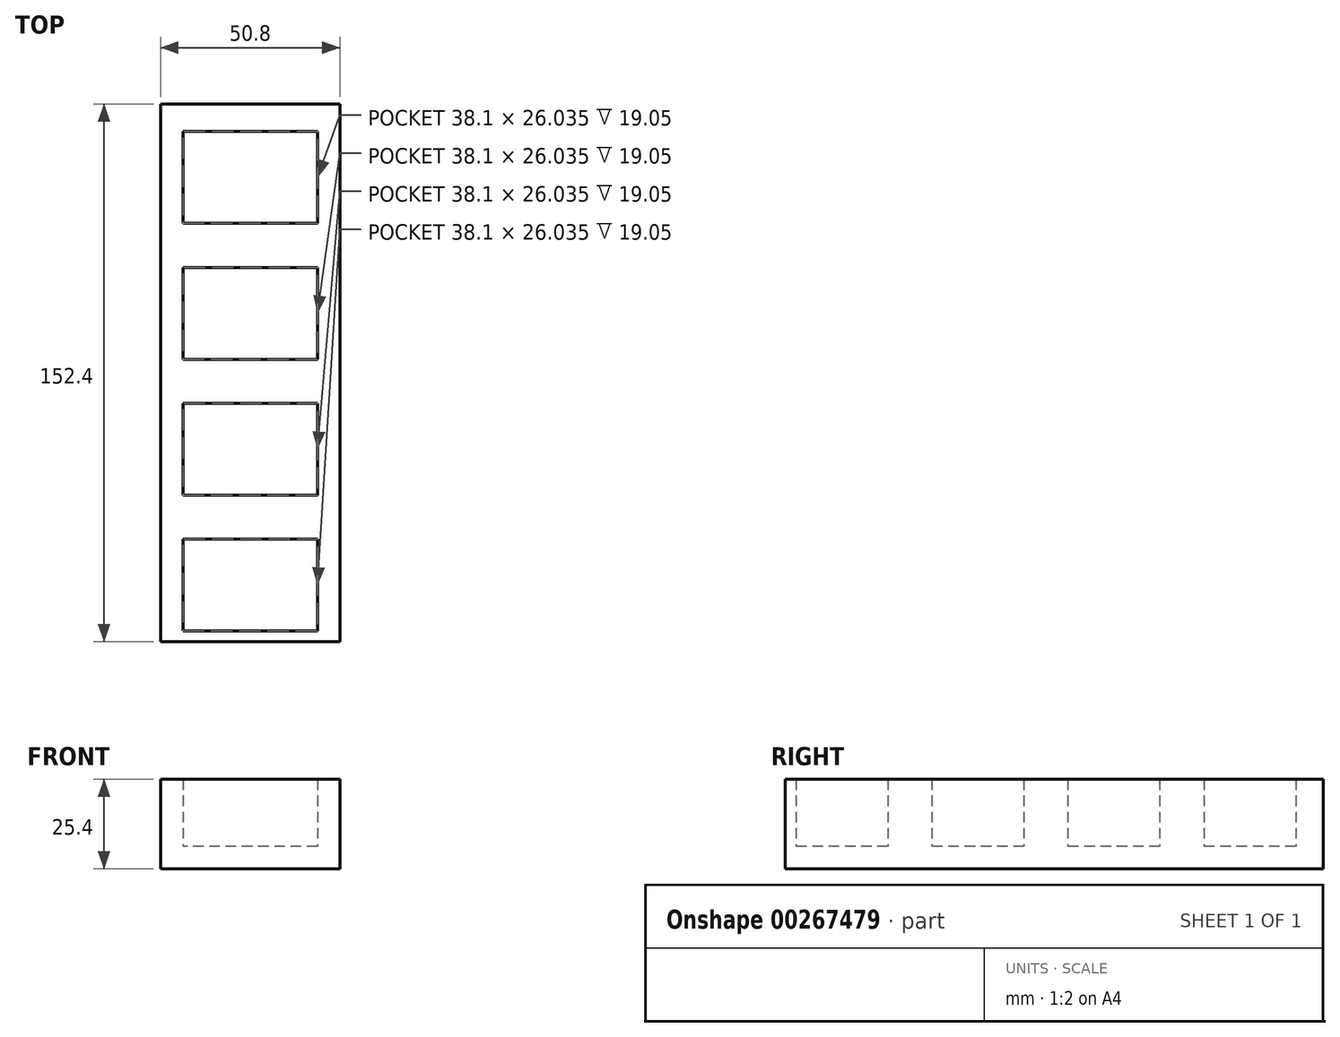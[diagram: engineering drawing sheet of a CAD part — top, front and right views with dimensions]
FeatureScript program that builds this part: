
annotation { "Feature Type Name" : "Feature", "Feature Type Description" : "" }
export const myFeature = defineFeature(function(context is Context, id is Id, definition is map)
    precondition{}
    {
        {
            var Q0;
            Q0=qCreatedBy(makeId("Top.planeOp"),FACE);
            var sketch = newSketch(context, id + "F0", { "sketchPlane" : qUnion([Q0])});
            skLineSegment(sketch, "E0.bottom", {"start": v(25.4, 76.2) * mm, "end": v(-25.4, 76.2) * mm});
            skLineSegment(sketch, "E0.top", {"start": v(25.4, -76.2) * mm, "end": v(-25.4, -76.2) * mm});
            skLineSegment(sketch, "E0.left", {"start": v(25.4, 76.2) * mm, "end": v(25.4, -76.2) * mm});
            skLineSegment(sketch, "E0.right", {"start": v(-25.4, 76.2) * mm, "end": v(-25.4, -76.2) * mm});
            skPoint(sketch, "E0.middle", {"position": v(0, 0) * mm});
            skLineSegment(sketch, "E1", {"start": v(0, 76.2) * mm, "end": v(0, 68.58) * mm});
            skPoint(sketch, "E1.endSnap0", {"position": v(0, 76.2) * mm});
            skLineSegment(sketch, "E2.bottom", {"start": v(19.05, 68.41) * mm, "end": v(-19.05, 68.41) * mm});
            skLineSegment(sketch, "E2.top", {"start": v(19.05, 42.38) * mm, "end": v(-19.05, 42.38) * mm});
            skLineSegment(sketch, "E2.left", {"start": v(19.05, 68.41) * mm, "end": v(19.05, 42.38) * mm});
            skLineSegment(sketch, "E2.right", {"start": v(-19.05, 68.41) * mm, "end": v(-19.05, 42.38) * mm});
            skPoint(sketch, "E2.middle", {"position": v(0, 55.4) * mm});
            skLineSegment(sketch, "E3", {"start": v(0, 42.38) * mm, "end": v(0, 29.68) * mm});
            skLineSegment(sketch, "E4.bottom", {"start": v(19.05, 29.9) * mm, "end": v(-19.05, 29.9) * mm});
            skLineSegment(sketch, "E4.top", {"start": v(19.05, 3.87) * mm, "end": v(-19.05, 3.87) * mm});
            skLineSegment(sketch, "E4.left", {"start": v(19.05, 29.9) * mm, "end": v(19.05, 3.87) * mm});
            skLineSegment(sketch, "E4.right", {"start": v(-19.05, 29.9) * mm, "end": v(-19.05, 3.87) * mm});
            skPoint(sketch, "E4.middle", {"position": v(0, 16.89) * mm});
            skLineSegment(sketch, "E5", {"start": v(0, 55.4) * mm, "end": v(0, 16.89) * mm});
            skLineSegment(sketch, "E6", {"start": v(0, 16.89) * mm, "end": v(0, -21.62) * mm});
            skLineSegment(sketch, "E7.bottom", {"start": v(19.05, -8.6) * mm, "end": v(-19.05, -8.6) * mm});
            skLineSegment(sketch, "E7.top", {"start": v(19.05, -34.63) * mm, "end": v(-19.05, -34.63) * mm});
            skLineSegment(sketch, "E7.left", {"start": v(19.05, -8.6) * mm, "end": v(19.05, -34.63) * mm});
            skLineSegment(sketch, "E7.right", {"start": v(-19.05, -8.6) * mm, "end": v(-19.05, -34.63) * mm});
            skPoint(sketch, "E7.middle", {"position": v(0, -21.62) * mm});
            skLineSegment(sketch, "E8", {"start": v(0, -21.62) * mm, "end": v(0, -60.12) * mm});
            skPoint(sketch, "E8.endSnap0", {"position": v(0, -34.63) * mm});
            skLineSegment(sketch, "E9.bottom", {"start": v(19.05, -47.1) * mm, "end": v(-19.05, -47.1) * mm});
            skLineSegment(sketch, "E9.top", {"start": v(19.05, -73.14) * mm, "end": v(-19.05, -73.14) * mm});
            skLineSegment(sketch, "E9.left", {"start": v(19.05, -47.1) * mm, "end": v(19.05, -73.14) * mm});
            skLineSegment(sketch, "E9.right", {"start": v(-19.05, -47.1) * mm, "end": v(-19.05, -73.14) * mm});
            skPoint(sketch, "E9.middle", {"position": v(0, -60.12) * mm});
            skSolve(sketch);
        }
        {
            var Q0;
            Q0=makeQuery(id+"F0.imprint","IMPRINT",FACE,{"disambiguationData":[TD([[makeQuery(id+"F0.imprint","IMPRINT",EDGE,{"derivedFrom":sQuery(id+"F0.wireOp",EDGE,"E0.top")}),-1.0]])]});
            extrude(context, id + "F1", {"entities" : qUnion([Q0]), "depth" : 25.4 * mm});
        }
        {
            var Q0;
            Q0=makeQuery(id+"F0.imprint","IMPRINT",FACE,{"disambiguationData":[TD([[makeQuery(id+"F0.imprint","IMPRINT",EDGE,{"derivedFrom":sQuery(id+"F0.wireOp",EDGE,"E2.bottom")}),1.0]])]});
            var Q1;
            {var subQ4=sQuery(id+"F0.wireOp",EDGE,"E4.left");Q1=makeQuery(id+"F0.imprint","IMPRINT",FACE,{"disambiguationData":[TD([[makeQuery(id+"F0.imprint","IMPRINT",EDGE,{"derivedFrom":subQ4}),-1.0]])]});}
            var Q2;
            {var subQ4=sQuery(id+"F0.wireOp",EDGE,"E4.right");Q2=makeQuery(id+"F0.imprint","IMPRINT",FACE,{"disambiguationData":[TD([[makeQuery(id+"F0.imprint","IMPRINT",EDGE,{"derivedFrom":subQ4}),1.0]])]});}
            var Q3;
            {var subQ0=sQuery(id+"F0.wireOp",EDGE,"E7.right");Q3=makeQuery(id+"F0.imprint","IMPRINT",FACE,{"disambiguationData":[TD([[makeQuery(id+"F0.imprint","IMPRINT",EDGE,{"derivedFrom":subQ0}),1.0]])]});}
            var Q4;
            {var subQ0=sQuery(id+"F0.wireOp",EDGE,"E7.left");Q4=makeQuery(id+"F0.imprint","IMPRINT",FACE,{"disambiguationData":[TD([[makeQuery(id+"F0.imprint","IMPRINT",EDGE,{"derivedFrom":subQ0}),-1.0]])]});}
            var Q5;
            Q5=makeQuery(id+"F0.imprint","IMPRINT",FACE,{"disambiguationData":[TD([[makeQuery(id+"F0.imprint","IMPRINT",EDGE,{"derivedFrom":sQuery(id+"F0.wireOp",EDGE,"E9.top")}),-1.0]])]});
            extrude(context, id + "F2", {"entities" : qUnion([Q0, Q1, Q2, Q3, Q4, Q5]), "operationType" : NewBodyOperationType.ADD, "depth" : 6.35 * mm});
        }
    });
